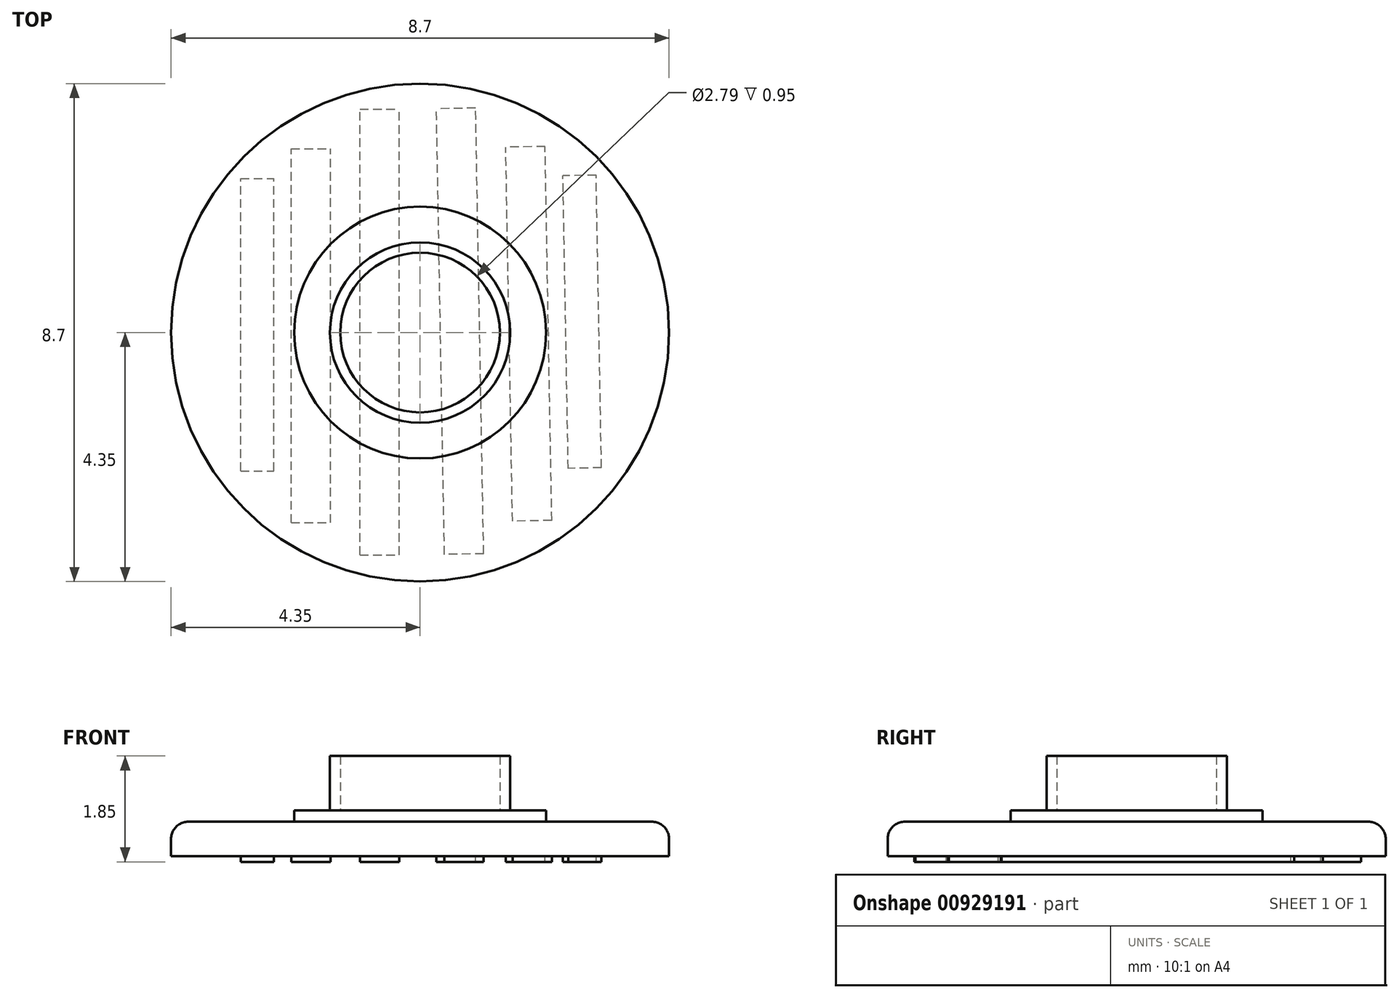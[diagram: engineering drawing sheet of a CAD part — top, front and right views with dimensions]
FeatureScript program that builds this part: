
annotation { "Feature Type Name" : "Feature", "Feature Type Description" : "" }
export const myFeature = defineFeature(function(context is Context, id is Id, definition is map)
    precondition{}
    {
        {
            var Q0;
            Q0=qCreatedBy(makeId("Top.planeOp"),FACE);
            var sketch = newSketch(context, id + "F0", { "sketchPlane" : qUnion([Q0])});
            skCircle(sketch, "E0", {"center": v(0, 0) * mm, "radius": 4.35 * mm});
            skSolve(sketch);
        }
        {
            var Q0;
            Q0=qSketchRegion(id+"F0",true);
            extrude(context, id + "F1", {"entities" : qUnion([Q0]), "depth" : 0.6 * mm, "offsetDistance" : 25 * mm});
        }
        {
            var Q0;
            Q0=makeQuery(id+"F1.opExtrude","CAP_FACE",FACE,{"disambiguationData":[OSD([sQuery(id+"F0.wireOp",EDGE,"E0")])],"isStart":false});
            var sketch = newSketch(context, id + "F2", { "sketchPlane" : qUnion([Q0])});
            skCircle(sketch, "E1", {"center": v(0, 0) * mm, "radius": 2.2 * mm});
            skSolve(sketch);
        }
        {
            var Q0;
            Q0=qSketchRegion(id+"F2",true);
            extrude(context, id + "F3", {"entities" : qUnion([Q0]), "operationType" : NewBodyOperationType.ADD, "depth" : 0.2 * mm, "offsetDistance" : 25 * mm});
        }
        {
            var Q0;
            Q0=makeQuery(id+"F3.opExtrude","CAP_FACE",FACE,{"disambiguationData":[OSD([sQuery(id+"F2.wireOp",EDGE,"E1")])],"isStart":false});
            var sketch = newSketch(context, id + "F4", { "sketchPlane" : qUnion([Q0])});
            skCircle(sketch, "E2", {"center": v(0, 0) * mm, "radius": 1.57 * mm});
            skCircle(sketch, "E3.0", {"center": v(0, 0) * mm, "radius": 1.4 * mm});
            skSolve(sketch);
        }
        {
            var Q0;
            Q0=makeQuery(id+"F4.imprint","IMPRINT",FACE,{"disambiguationData":[TD([[makeQuery(id+"F4.imprint","IMPRINT",EDGE,{"derivedFrom":sQuery(id+"F4.wireOp",EDGE,"E2")}),1.0]])]});
            extrude(context, id + "F5", {"entities" : qUnion([Q0]), "operationType" : NewBodyOperationType.ADD, "depth" : 0.95 * mm, "offsetDistance" : 25 * mm});
        }
        {
            var Q0;
            Q0=makeQuery(id+"F1.opExtrude","CAP_EDGE",EDGE,{"disambiguationData":[OSD([sQuery(id+"F0.wireOp",EDGE,"E0")])],"isStart":false});
            fillet(context, id + "F6", {"entities" : qUnion([Q0]), "radius" : 0.3 * mm, "tangentPropagation" : true, "allowEdgeOverflow" : false});
        }
        {
            var Q0;
            Q0=makeQuery(id+"F1.opExtrude","CAP_FACE",FACE,{"disambiguationData":[OSD([sQuery(id+"F0.wireOp",EDGE,"E0")])],"isStart":true});
            var sketch = newSketch(context, id + "F7", { "sketchPlane" : qUnion([Q0])});
            skLineSegment(sketch, "E4.bottom", {"start": v(-3.13, 2.42) * mm, "end": v(-2.55, 2.42) * mm});
            skLineSegment(sketch, "E4.top", {"start": v(-3.13, -2.7) * mm, "end": v(-2.55, -2.7) * mm});
            skLineSegment(sketch, "E4.left", {"start": v(-3.13, 2.42) * mm, "end": v(-3.13, -2.7) * mm});
            skLineSegment(sketch, "E4.right", {"start": v(-2.55, 2.42) * mm, "end": v(-2.55, -2.7) * mm});
            skLineSegment(sketch, "E5.bottom", {"start": v(-2.25, 3.32) * mm, "end": v(-1.56, 3.32) * mm});
            skLineSegment(sketch, "E5.top", {"start": v(-2.25, -3.21) * mm, "end": v(-1.56, -3.21) * mm});
            skLineSegment(sketch, "E5.left", {"start": v(-2.25, 3.32) * mm, "end": v(-2.25, -3.21) * mm});
            skLineSegment(sketch, "E5.right", {"start": v(-1.56, 3.32) * mm, "end": v(-1.56, -3.21) * mm});
            skLineSegment(sketch, "E6.bottom", {"start": v(-1.05, 3.89) * mm, "end": v(-0.37, 3.89) * mm});
            skLineSegment(sketch, "E6.top", {"start": v(-1.05, -3.9) * mm, "end": v(-0.37, -3.9) * mm});
            skLineSegment(sketch, "E6.left", {"start": v(-1.05, 3.89) * mm, "end": v(-1.05, -3.9) * mm});
            skLineSegment(sketch, "E6.right", {"start": v(-0.37, 3.89) * mm, "end": v(-0.37, -3.9) * mm});
            skLineSegment(sketch, "E7.MirrorCS", {"start": v(0.43, 3.88) * mm, "end": v(0.29, -3.91) * mm});
            skLineSegment(sketch, "E8.MirrorCS", {"start": v(1.11, 3.87) * mm, "end": v(0.43, 3.88) * mm});
            skLineSegment(sketch, "E9.MirrorCS", {"start": v(1.11, 3.87) * mm, "end": v(0.97, -3.92) * mm});
            skLineSegment(sketch, "E10.MirrorCS", {"start": v(0.97, -3.92) * mm, "end": v(0.29, -3.91) * mm});
            skLineSegment(sketch, "E11.MirrorCS", {"start": v(2.18, -3.25) * mm, "end": v(1.5, -3.24) * mm});
            skLineSegment(sketch, "E12.MirrorCS", {"start": v(2.3, 3.28) * mm, "end": v(2.18, -3.25) * mm});
            skLineSegment(sketch, "E13.MirrorCS", {"start": v(1.61, 3.3) * mm, "end": v(1.5, -3.24) * mm});
            skLineSegment(sketch, "E14.MirrorCS", {"start": v(2.3, 3.28) * mm, "end": v(1.61, 3.3) * mm});
            skLineSegment(sketch, "E15.MirrorCS", {"start": v(2.59, 2.37) * mm, "end": v(2.5, -2.74) * mm});
            skLineSegment(sketch, "E16.MirrorCS", {"start": v(3.17, 2.36) * mm, "end": v(2.59, 2.37) * mm});
            skLineSegment(sketch, "E17.MirrorCS", {"start": v(3.17, 2.36) * mm, "end": v(3.08, -2.75) * mm});
            skLineSegment(sketch, "E18.MirrorCS", {"start": v(3.08, -2.75) * mm, "end": v(2.5, -2.74) * mm});
            skPoint(sketch, "E19.end.orphan", {"position": v(0, 0.52) * mm});
            skSolve(sketch);
        }
        {
            var Q0;
            Q0=makeQuery(id+"F7.imprint","IMPRINT",FACE,{"disambiguationData":[TD([[makeQuery(id+"F7.imprint","IMPRINT",EDGE,{"derivedFrom":sQuery(id+"F7.wireOp",EDGE,"E4.bottom")}),-1.0]])]});
            var Q1;
            Q1=makeQuery(id+"F7.imprint","IMPRINT",FACE,{"disambiguationData":[TD([[makeQuery(id+"F7.imprint","IMPRINT",EDGE,{"derivedFrom":sQuery(id+"F7.wireOp",EDGE,"E5.bottom")}),-1.0]])]});
            var Q2;
            Q2=makeQuery(id+"F7.imprint","IMPRINT",FACE,{"disambiguationData":[TD([[makeQuery(id+"F7.imprint","IMPRINT",EDGE,{"derivedFrom":sQuery(id+"F7.wireOp",EDGE,"E6.bottom")}),-1.0]])]});
            var Q3;
            Q3=makeQuery(id+"F7.imprint","IMPRINT",FACE,{"disambiguationData":[TD([[makeQuery(id+"F7.imprint","IMPRINT",EDGE,{"derivedFrom":sQuery(id+"F7.wireOp",EDGE,"E7.MirrorCS")}),1.0]])]});
            var Q4;
            Q4=makeQuery(id+"F7.imprint","IMPRINT",FACE,{"disambiguationData":[TD([[makeQuery(id+"F7.imprint","IMPRINT",EDGE,{"derivedFrom":sQuery(id+"F7.wireOp",EDGE,"E11.MirrorCS")}),-1.0]])]});
            var Q5;
            Q5=makeQuery(id+"F7.imprint","IMPRINT",FACE,{"disambiguationData":[TD([[makeQuery(id+"F7.imprint","IMPRINT",EDGE,{"derivedFrom":sQuery(id+"F7.wireOp",EDGE,"E15.MirrorCS")}),1.0]])]});
            extrude(context, id + "F8", {"entities" : qUnion([Q0, Q1, Q2, Q3, Q4, Q5]), "operationType" : NewBodyOperationType.ADD, "depth" : 0.1 * mm, "offsetDistance" : 25 * mm});
        }
    });
